# Revit family: Water_Heater-Haws-AXION_Steam_Water_Heater-9400
name_source: partatom
category: Mechanical Equipment
revit_build: Autodesk Revit Architecture 2013 (Build: 20130531_2115(x64)
units: mm (PartAtom-declared; Revit-internal decimal feet)

## types (1)
- 9400
    Default Elevation = 4' - 0"
    Description = Steam Water Heater
    Flow Rate = 25 GPM
    Inlet Steam Pressure = 60.00 psi
    Inlet Water Pressure = 90.00 psi
    Inlet Water Temperature = 80 °F
    Installation Drawing = http://www.hawsco.com
    Manufacturer = Haws
    Metal = Metal - Haws - Brass
    Model = 9400
    Operating Temperature = 120 °F
    Operation Maintenance Manual = http://www.hawsco.com
    Plastic = Plastic - Haws - Yellow
    Product Documentation Link = http://www.hawsco.com
    Product Name = AXION Steam Water Heater
    Product Page URL = http://www.hawsco.com
    Steam Temperature = 350 °F
    URL = http://www.hawsco.com
    Warranty = http://www.hawsco.com

## geometry (parser evidence)
native form markers: Blend x8, Sweep x4
no freeform markers — native parametric forms only
